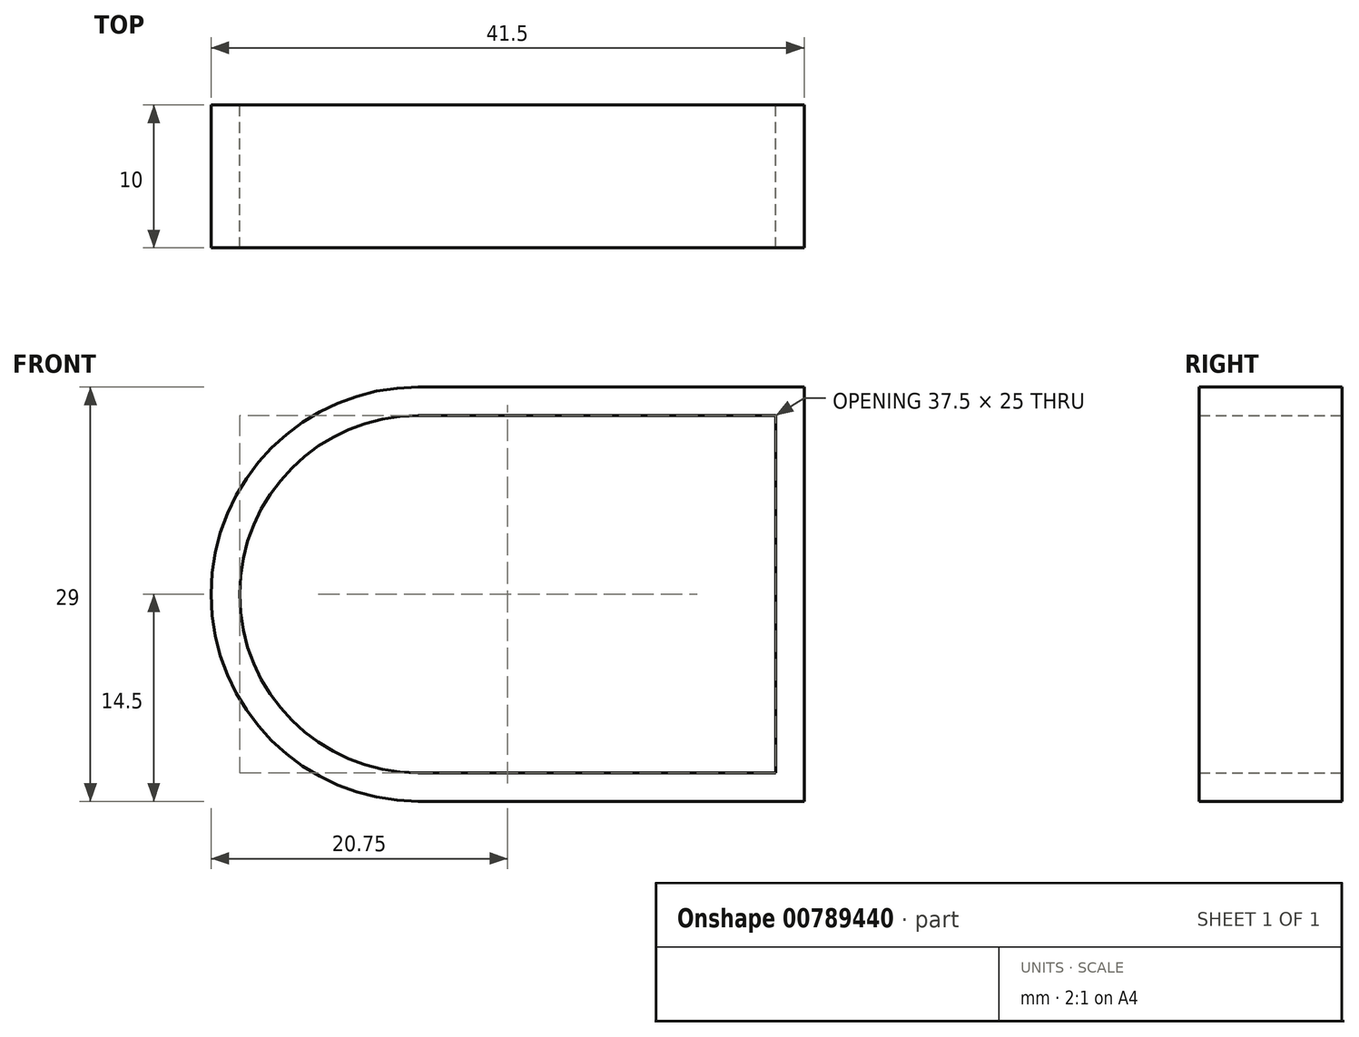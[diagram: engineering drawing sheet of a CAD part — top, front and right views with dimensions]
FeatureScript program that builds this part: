
annotation { "Feature Type Name" : "Feature", "Feature Type Description" : "" }
export const myFeature = defineFeature(function(context is Context, id is Id, definition is map)
    precondition{}
    {
        {
            var Q0;
            Q0=qCreatedBy(makeId("Front.planeOp"),FACE);
            var sketch = newSketch(context, id + "F0", { "sketchPlane" : qUnion([Q0])});
            skLineSegment(sketch, "E0.bottom", {"start": v(0, 0) * mm, "end": v(25, 0) * mm});
            skLineSegment(sketch, "E0.top", {"start": v(0, 25) * mm, "end": v(25, 25) * mm});
            skLineSegment(sketch, "E0.right", {"start": v(25, 0) * mm, "end": v(25, 25) * mm});
            skArc(sketch, "E1", {"start": v(0, 25) * mm, "mid": v(-12.5, 12.5) * mm, "end": v(0, 0) * mm});
            skLineSegment(sketch, "E2.0", {"start": v(0, 27) * mm, "end": v(27, 27) * mm});
            skArc(sketch, "E2.1", {"start": v(0, 27) * mm, "mid": v(-14.5, 12.5) * mm, "end": v(0, -2) * mm});
            skLineSegment(sketch, "E2.2", {"start": v(0, -2) * mm, "end": v(27, -2) * mm});
            skLineSegment(sketch, "E2.3", {"start": v(27, -2) * mm, "end": v(27, 27) * mm});
            skSolve(sketch);
        }
        {
            var Q0;
            Q0=makeQuery(id+"F0.imprint","IMPRINT",FACE,{"disambiguationData":[TD([[makeQuery(id+"F0.imprint","IMPRINT",EDGE,{"derivedFrom":sQuery(id+"F0.wireOp",EDGE,"E0.bottom")}),-1.0]])]});
            extrude(context, id + "F1", {"entities" : qUnion([Q0]), "depth" : 10 * mm, "offsetDistance" : 25.4 * mm});
        }
    });
